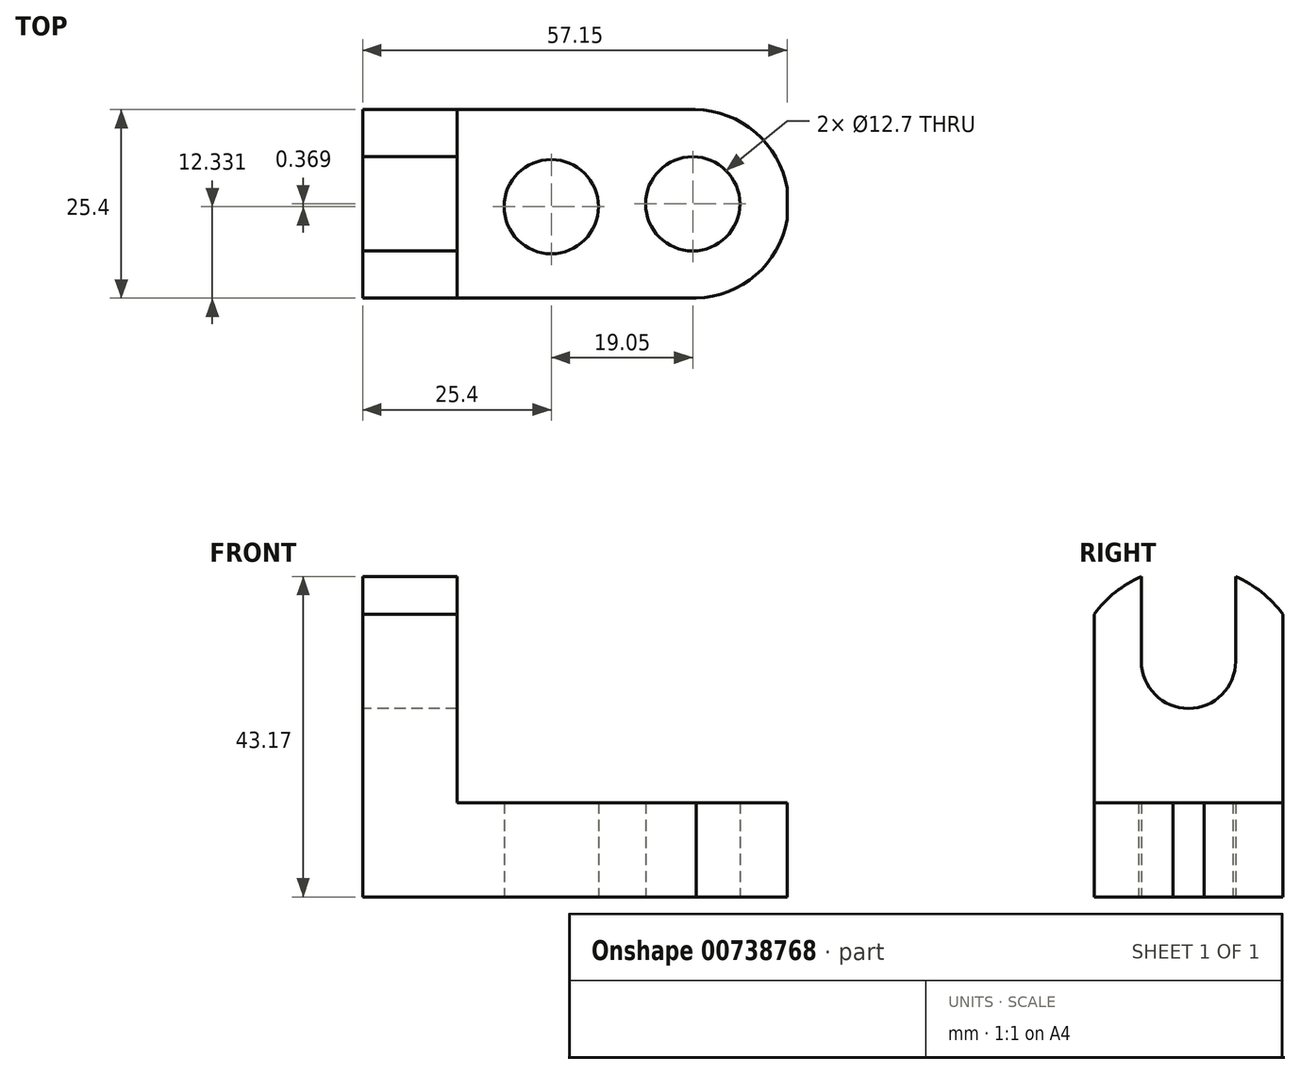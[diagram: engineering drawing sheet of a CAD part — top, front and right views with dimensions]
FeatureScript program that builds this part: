
annotation { "Feature Type Name" : "Feature", "Feature Type Description" : "" }
export const myFeature = defineFeature(function(context is Context, id is Id, definition is map)
    precondition{}
    {
        {
            var Q0;
            Q0=qCreatedBy(makeId("Front.planeOp"),FACE);
            var sketch = newSketch(context, id + "F0", { "sketchPlane" : qUnion([Q0])});
            skLineSegment(sketch, "E0", {"start": v(0, 0) * mm, "end": v(0, 44.45) * mm});
            skLineSegment(sketch, "E1", {"start": v(0, 44.45) * mm, "end": v(12.7, 44.45) * mm});
            skLineSegment(sketch, "E2", {"start": v(12.7, 44.45) * mm, "end": v(12.7, 12.7) * mm});
            skLineSegment(sketch, "E3", {"start": v(12.7, 12.7) * mm, "end": v(57.15, 12.7) * mm});
            skLineSegment(sketch, "E4", {"start": v(57.15, 12.7) * mm, "end": v(57.15, 0) * mm});
            skLineSegment(sketch, "E5", {"start": v(57.15, 0) * mm, "end": v(0, 0) * mm});
            skSolve(sketch);
        }
        {
            var Q0;
            Q0 = qSketchRegion(id + "F0", true);
            extrude(context, id + "F1", {"entities" : qUnion([Q0]), "depth" : 25.4 * mm, "offsetDistance" : 25.4 * mm});
        }
        {
            var Q0;
            Q0=qCreatedBy(makeId("Right.planeOp"),FACE);
            var sketch = newSketch(context, id + "F2", { "sketchPlane" : qUnion([Q0])});
            skLineSegment(sketch, "E6", {"start": v(-25.4, 31.75) * mm, "end": v(0, 31.75) * mm});
            skCircle(sketch, "E7", {"center": v(-12.7, 31.75) * mm, "radius": 6.35 * mm});
            skLineSegment(sketch, "E8", {"start": v(-19.05, 31.75) * mm, "end": v(-19.05, 44.45) * mm});
            skLineSegment(sketch, "E9", {"start": v(-6.35, 31.75) * mm, "end": v(-6.35, 44.45) * mm});
            skLineSegment(sketch, "E10", {"start": v(-19.05, 44.45) * mm, "end": v(-6.35, 44.45) * mm});
            skSolve(sketch);
        }
        {
            var Q0;
            Q0 = qSketchRegion(id + "F2", true);
            extrude(context, id + "F3", {"entities" : qUnion([Q0]), "operationType" : NewBodyOperationType.REMOVE, "endBound" : BoundingType.THROUGH_ALL, "depth" : 25.4 * mm, "offsetDistance" : 25.4 * mm});
        }
        {
            var Q0;
            Q0=qCreatedBy(makeId("Right.planeOp"),FACE);
            var sketch = newSketch(context, id + "F4", { "sketchPlane" : qUnion([Q0])});
            skLineSegment(sketch, "E11", {"start": v(-25.4, 38.1) * mm, "end": v(0, 38.1) * mm});
            skLineSegment(sketch, "E12", {"start": v(-25.4, 44.45) * mm, "end": v(0, 44.45) * mm});
            skArc(sketch, "E13", {"start": v(0, 38.1) * mm, "mid": v(-12.7, 44.5) * mm, "end": v(-25.4, 38.1) * mm});
            skLineSegment(sketch, "E14", {"start": v(-25.4, 38.1) * mm, "end": v(-25.4, 44.45) * mm});
            skLineSegment(sketch, "E15", {"start": v(0, 44.45) * mm, "end": v(0, 38.1) * mm});
            skSolve(sketch);
        }
        {
            var Q0;
            {var subQ0=sQuery(id+"F4.wireOp",EDGE,"E14");Q0=makeQuery(id+"F4.imprint","IMPRINT",FACE,{"disambiguationData":[TD([[makeQuery(id+"F4.imprint","IMPRINT",EDGE,{"derivedFrom":subQ0}),-1.0]])]});}
            var Q1;
            {var subQ0=sQuery(id+"F4.wireOp",EDGE,"E13");var subQ1=sQuery(id+"F4.wireOp",EDGE,"E12");var subQ2=makeQuery(id+"F4.imprint","INTERSECT",VERTEX,{"disambiguationData":[OD(0.0)],"derivedFrom":[subQ1,subQ0]});Q1=makeQuery(id+"F4.imprint","IMPRINT",FACE,{"disambiguationData":[TD([[makeQuery(id+"F4.imprint","IMPRINT",EDGE,{"disambiguationData":[TD([[subQ2,-1.0]])],"derivedFrom":subQ1}),1.0]])]});}
            var Q2;
            {var subQ0=sQuery(id+"F4.wireOp",EDGE,"E15");Q2=makeQuery(id+"F4.imprint","IMPRINT",FACE,{"disambiguationData":[TD([[makeQuery(id+"F4.imprint","IMPRINT",EDGE,{"derivedFrom":subQ0}),-1.0]])]});}
            extrude(context, id + "F5", {"entities" : qUnion([Q0, Q1, Q2]), "operationType" : NewBodyOperationType.REMOVE, "depth" : 25.4 * mm, "offsetDistance" : 25.4 * mm});
        }
        {
            var Q0;
            Q0=qCreatedBy(makeId("Top.planeOp"),FACE);
            var sketch = newSketch(context, id + "F6", { "sketchPlane" : qUnion([Q0])});
            skLineSegment(sketch, "E16", {"start": v(25.4, 0) * mm, "end": v(25.4, -26.14) * mm});
            skLineSegment(sketch, "E17", {"start": v(44.45, 0) * mm, "end": v(44.45, -25.4) * mm});
            skCircle(sketch, "E18", {"center": v(25.4, -13.07) * mm, "radius": 6.35 * mm});
            skCircle(sketch, "E19", {"center": v(44.45, -12.7) * mm, "radius": 6.35 * mm});
            skArc(sketch, "E20", {"start": v(44.45, -25.4) * mm, "mid": v(57.32, -12.7) * mm, "end": v(44.45, 0) * mm});
            skLineSegment(sketch, "E21", {"start": v(44.45, 0) * mm, "end": v(59.04, 0) * mm});
            skLineSegment(sketch, "E22", {"start": v(59.04, 0) * mm, "end": v(59.04, -25.31) * mm});
            skLineSegment(sketch, "E23", {"start": v(59.04, -25.31) * mm, "end": v(44.45, -25.4) * mm});
            skLineSegment(sketch, "E24", {"start": v(44.45, -25.4) * mm, "end": v(44.45, -26.15) * mm});
            skLineSegment(sketch, "E25", {"start": v(44.45, -26.15) * mm, "end": v(58.93, -26.07) * mm});
            skLineSegment(sketch, "E26", {"start": v(58.93, -26.07) * mm, "end": v(59.04, -25.31) * mm});
            skSolve(sketch);
        }
        {
            var Q0;
            {var subQ0=sQuery(id+"F6.wireOp",EDGE,"E18");var subQ1=sQuery(id+"F6.wireOp",EDGE,"E16");var subQ2=makeQuery(id+"F6.imprint","INTERSECT",VERTEX,{"disambiguationData":[OD(0.0)],"derivedFrom":[subQ1,subQ0]});Q0=makeQuery(id+"F6.imprint","IMPRINT",FACE,{"disambiguationData":[TD([[makeQuery(id+"F6.imprint","IMPRINT",EDGE,{"disambiguationData":[TD([[subQ2,1.0]])],"derivedFrom":subQ1}),-1.0]])]});}
            var Q1;
            {var subQ0=sQuery(id+"F6.wireOp",EDGE,"E18");var subQ1=sQuery(id+"F6.wireOp",EDGE,"E16");var subQ2=makeQuery(id+"F6.imprint","INTERSECT",VERTEX,{"disambiguationData":[OD(0.0)],"derivedFrom":[subQ1,subQ0]});Q1=makeQuery(id+"F6.imprint","IMPRINT",FACE,{"disambiguationData":[TD([[makeQuery(id+"F6.imprint","IMPRINT",EDGE,{"disambiguationData":[TD([[subQ2,1.0]])],"derivedFrom":subQ1}),1.0]])]});}
            var Q2;
            {var subQ0=sQuery(id+"F6.wireOp",EDGE,"E19");var subQ1=sQuery(id+"F6.wireOp",EDGE,"E17");var subQ2=makeQuery(id+"F6.imprint","INTERSECT",VERTEX,{"disambiguationData":[OD(0.0)],"derivedFrom":[subQ1,subQ0]});Q2=makeQuery(id+"F6.imprint","IMPRINT",FACE,{"disambiguationData":[TD([[makeQuery(id+"F6.imprint","IMPRINT",EDGE,{"disambiguationData":[TD([[subQ2,-1.0]])],"derivedFrom":subQ1}),-1.0]])]});}
            var Q3;
            {var subQ0=sQuery(id+"F6.wireOp",EDGE,"E23");var subQ1=sQuery(id+"F6.wireOp",EDGE,"E20");var subQ3=makeQuery(id+"F6.imprint","INTERSECT",VERTEX,{"derivedFrom":[subQ1,subQ0]});Q3=makeQuery(id+"F6.imprint","IMPRINT",FACE,{"disambiguationData":[TD([[makeQuery(id+"F6.imprint","IMPRINT",EDGE,{"disambiguationData":[TD([[subQ3,1.0]])],"derivedFrom":subQ1}),1.0]])]});}
            var Q4;
            {var subQ0=sQuery(id+"F6.wireOp",EDGE,"E21");var subQ1=sQuery(id+"F6.wireOp",EDGE,"E20");var subQ3=makeQuery(id+"F6.imprint","INTERSECT",VERTEX,{"derivedFrom":[subQ1,subQ0]});Q4=makeQuery(id+"F6.imprint","IMPRINT",FACE,{"disambiguationData":[TD([[makeQuery(id+"F6.imprint","IMPRINT",EDGE,{"disambiguationData":[TD([[subQ3,-1.0]])],"derivedFrom":subQ1}),1.0]])]});}
            var Q5;
            {var subQ0=sQuery(id+"F6.wireOp",EDGE,"E19");var subQ1=sQuery(id+"F6.wireOp",EDGE,"E17");var subQ2=makeQuery(id+"F6.imprint","INTERSECT",VERTEX,{"disambiguationData":[OD(0.0)],"derivedFrom":[subQ1,subQ0]});Q5=makeQuery(id+"F6.imprint","IMPRINT",FACE,{"disambiguationData":[TD([[makeQuery(id+"F6.imprint","IMPRINT",EDGE,{"disambiguationData":[TD([[subQ2,-1.0]])],"derivedFrom":subQ1}),1.0]])]});}
            var Q6;
            {var subQ5=sQuery(id+"F6.wireOp",EDGE,"E22");Q6=makeQuery(id+"F6.imprint","IMPRINT",FACE,{"disambiguationData":[TD([[makeQuery(id+"F6.imprint","IMPRINT",EDGE,{"derivedFrom":subQ5}),-1.0]])]});}
            var Q7;
            {var subQ0=sQuery(id+"F6.wireOp",EDGE,"E24");Q7=makeQuery(id+"F6.imprint","IMPRINT",FACE,{"disambiguationData":[TD([[makeQuery(id+"F6.imprint","IMPRINT",EDGE,{"derivedFrom":subQ0}),1.0]])]});}
            extrude(context, id + "F7", {"entities" : qUnion([Q0, Q1, Q2, Q3, Q4, Q5, Q6, Q7]), "operationType" : NewBodyOperationType.REMOVE, "endBound" : BoundingType.THROUGH_ALL, "depth" : 25.4 * mm, "offsetDistance" : 25.4 * mm});
        }
    });
